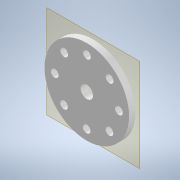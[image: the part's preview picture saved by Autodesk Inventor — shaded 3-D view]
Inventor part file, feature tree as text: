
AUTODESK INVENTOR PART (.ipt)
format: ipt  version: 2021 (Build 250183000, 183)  size: 119,808 bytes
history: native  units: mm
features: other x2, plane x1, extrude x1, sketch x1, reference x1
ambient origin geometry x8: Origin, YZ Plane, XZ Plane, XY Plane, X Axis, Y Axis, Z Axis, Center Point
bodies: Solid1 (feature_tree)
feature tree (6):
  plane  "Work Plane1"
  extrude  "Extrusion1"  [1 undecoded]
  sketch  "Sketch1"  dims[d0=3.0mm d1=0.0mm]
  reference  "Reference1"
  other  "4_WheelsSwerve01.iam"
  other  "wheel(Mirror)(Mirror):1"
note: 1 required parameter value undecoded (feature->parameter linkage not recoverable at this tier; creation-order binding heuristic only, values carry confidence <= 0.55)
